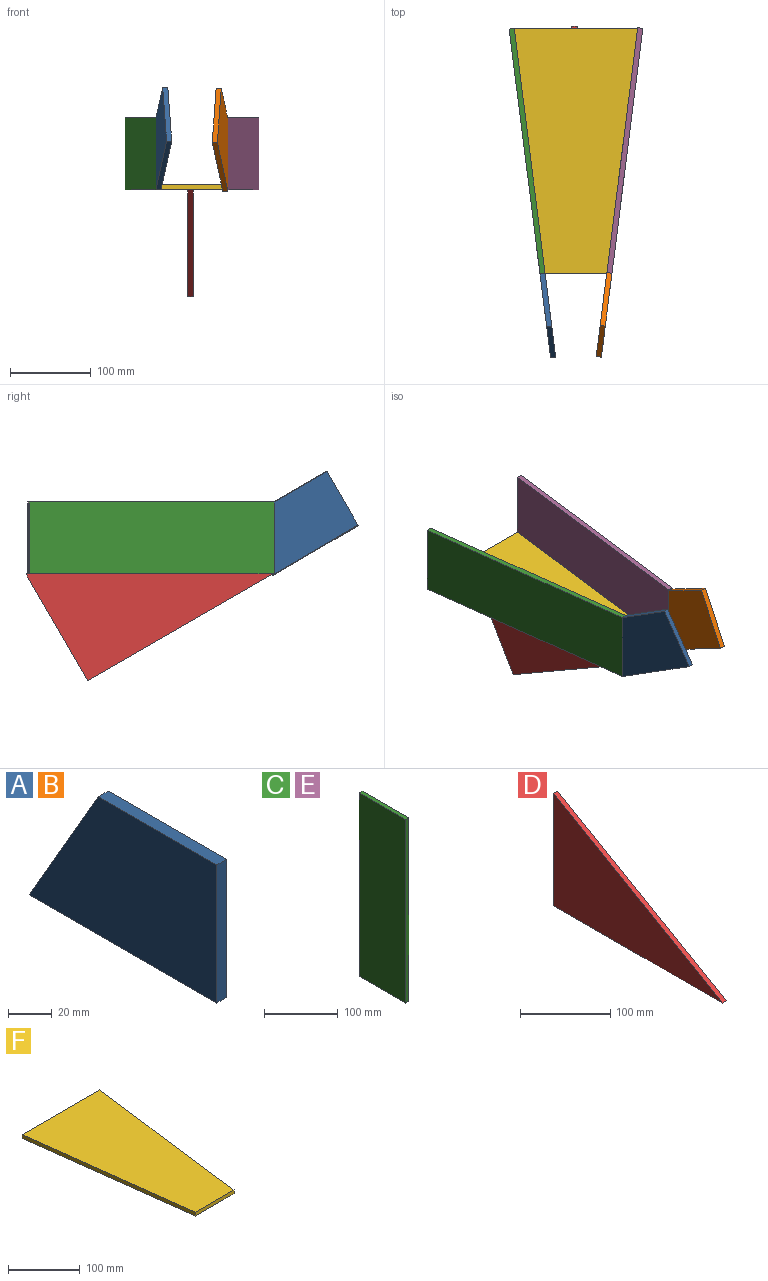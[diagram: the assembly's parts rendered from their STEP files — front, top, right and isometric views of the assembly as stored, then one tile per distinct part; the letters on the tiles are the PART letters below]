
ASSEMBLY  parts=6 mates=7
PART A: 6 faces, bbox 6.4x120.7x77 mm
  f0: plane 76.99x6.35mm, normal (0,-1,0), area 488.9mm2, adj f1,f3,f4,f5
  f1: plane 120.65x6.35mm, normal (0,0,-1), area 766.1mm2, adj f0,f2,f4,f5
  f2: plane 76.99x44.45mm, normal (0,0.87,0.5), area 564.5mm2, adj f1,f3,f4,f5
  f3: plane 76.2x6.35mm, normal (0,0,1), area 483.9mm2, adj f0,f2,f4,f5
  f4: plane 120.65x76.99mm, normal (1,0,0), area 7577.7mm2, adj f0,f1,f2,f3
  f5: plane 120.65x76.99mm, normal (-1,0,0), area 7577.7mm2, adj f0,f1,f2,f3
PART B: same geometry as A
PART C: 6 faces, bbox 6.4x88.9x304.8 mm
  f0: plane 304.8x88.9mm, normal (-1,0,0), area 27096.7mm2, adj f1,f3,f4,f5
  f1: plane 304.8x6.35mm, normal (0,-1,0), area 1935.5mm2, adj f0,f2,f4,f5
  f2: plane 304.8x88.9mm, normal (1,0,0), area 27096.7mm2, adj f1,f3,f4,f5
  f3: plane 304.8x6.35mm, normal (0,1,0), area 1935.5mm2, adj f0,f2,f4,f5
  f4: plane 88.9x6.35mm, normal (0,0,1), area 564.5mm2, adj f0,f1,f2,f3
  f5: plane 88.9x6.35mm, normal (0,0,-1), area 564.5mm2, adj f0,f1,f2,f3
PART D: 5 faces, bbox 6.4x264x152.4 mm
  f0: plane 263.96x152.4mm, normal (0,-0.5,0.87), area 1935.5mm2, adj f1,f2,f3,f4
  f1: plane 263.96x6.35mm, normal (0,0,-1), area 1676.2mm2, adj f0,f2,f3,f4
  f2: plane 152.4x6.35mm, normal (0,1,0), area 967.7mm2, adj f0,f1,f3,f4
  f3: plane 263.96x152.4mm, normal (1,0,0), area 20114.1mm2, adj f0,f1,f2
  f4: plane 263.96x152.4mm, normal (-1,0,0), area 20114.1mm2, adj f0,f1,f2
PART E: same geometry as C
PART F: 6 faces, bbox 152.4x302.4x6.4 mm
  f0: plane 302.41x38.1mm, normal (-0.99,-0.12,0), area 1935.5mm2, adj f1,f3,f4,f5
  f1: plane 76.2x6.35mm, normal (0,-1,0), area 483.9mm2, adj f0,f2,f4,f5
  f2: plane 302.41x38.1mm, normal (0.99,-0.12,0), area 1935.5mm2, adj f1,f3,f4,f5
  f3: plane 152.4x6.35mm, normal (0,1,0), area 967.7mm2, adj f0,f2,f4,f5
  f4: plane 302.41x152.4mm, normal (0,0,1), area 34565.4mm2, adj f0,f1,f2,f3
  f5: plane 302.41x152.4mm, normal (0,0,-1), area 34565.4mm2, adj f0,f1,f2,f3
PLACE A rot(axis=(-0.97,-0.06,0.23),30.8deg) t=(37.91,-180.39,116.79)mm
PLACE B rot(axis=(-0.97,0.06,-0.23),30.8deg) t=(94.28,-178.68,115.31)mm
PLACE C rot(axis=(-1,-0.06,0.06),90.2deg) t=(24.84,-76.72,145.37)mm
PLACE D rot(axis=(-1,0,0),30deg) t=(64.26,-75.18,56.47)mm
PLACE E rot(axis=(-1,0.06,-0.06),90.2deg) t=(107.43,-75.02,145.37)mm
PLACE F t=(31.13,-75.79,56.47)mm
MATE planar A.f2 <-> C.f5  axis (-0.13,0.99,0) through (27.99,-76.32,100.92)mm
MATE planar E.f3 <-> F.f5  axis (0,0,-1) through (129.63,75.79,56.47)mm
MATE planar C.f2 <-> F.f0  axis (0.99,0.12,0) through (12.09,75.28,56.47)mm
MATE planar D.f0 <-> F.f5  axis (0,0,1) through (67.43,77.22,56.47)mm
MATE planar E.f0 <-> F.f2  axis (-0.99,0.12,0) through (126.48,76.18,100.92)mm
MATE planar B.f2 <-> E.f5  axis (0.13,0.99,0) through (107.35,-75.01,99.43)mm
MATE planar C.f3 <-> F.f5  axis (0,0,-1) through (8.94,74.88,56.47)mm
